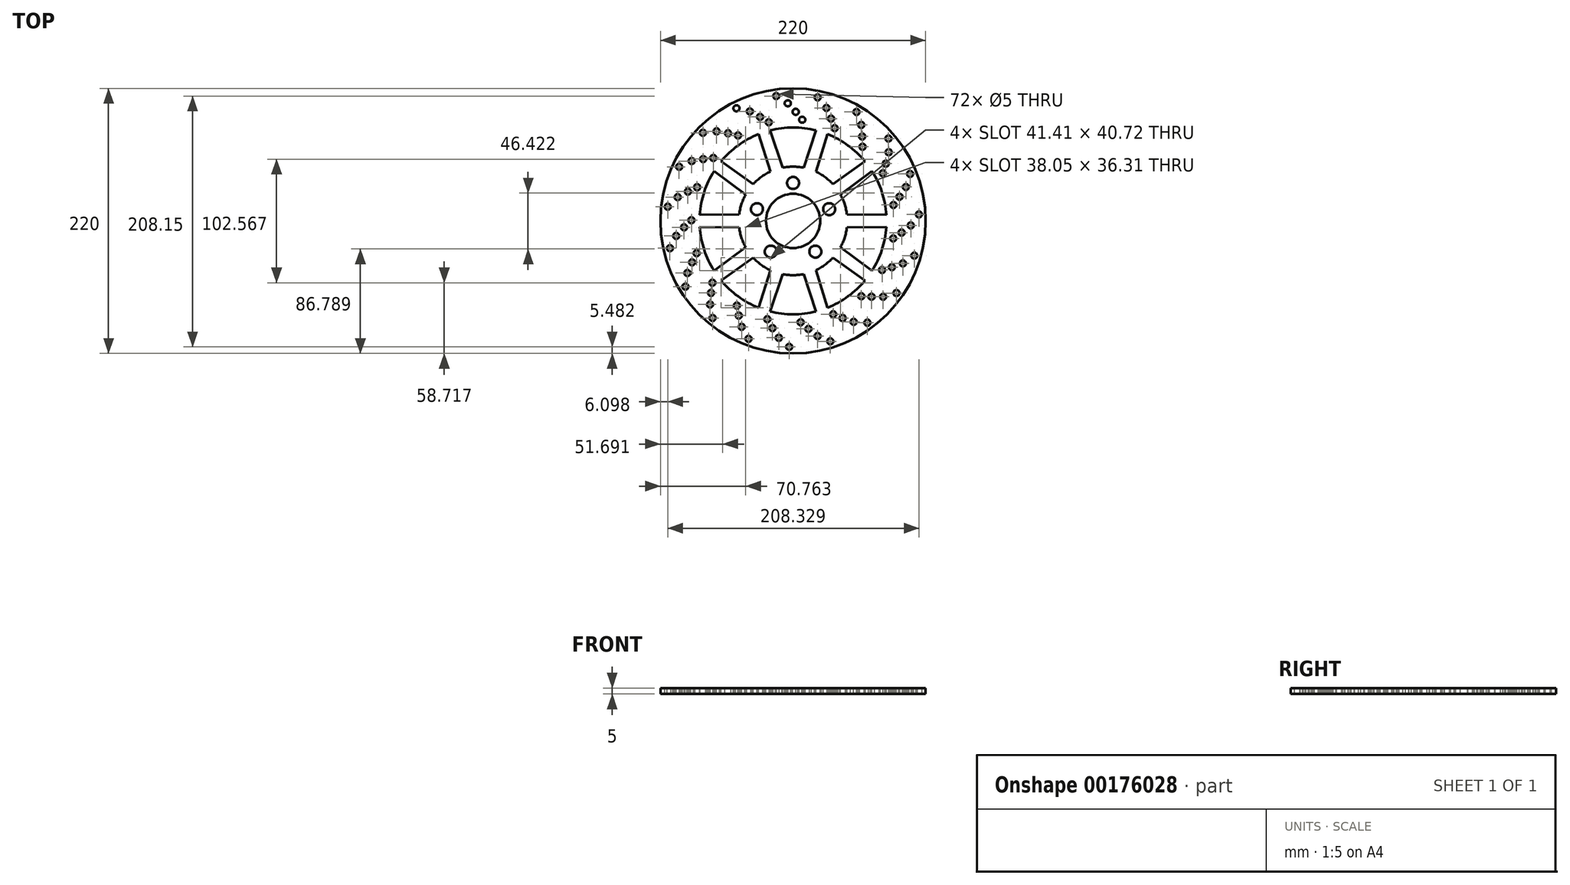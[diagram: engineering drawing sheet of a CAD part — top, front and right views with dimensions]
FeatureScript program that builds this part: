
annotation { "Feature Type Name" : "Feature", "Feature Type Description" : "" }
export const myFeature = defineFeature(function(context is Context, id is Id, definition is map)
    precondition{}
    {
        {
            var Q0;
            Q0=qCreatedBy(makeId("Top.planeOp"),FACE);
            var sketch = newSketch(context, id + "F0", { "sketchPlane" : qUnion([Q0])});
            skCircle(sketch, "E0", {"center": v(0, 0) * mm, "radius": 110 * mm});
            skSolve(sketch);
        }
        {
            var Q0;
            Q0 = qSketchRegion(id + "F0", true);
            extrude(context, id + "F1", {"entities" : qUnion([Q0]), "depth" : 5 * mm});
        }
        {
            var Q0;
            Q0=makeQuery(id+"F1.opExtrude","CAP_FACE",FACE,{"disambiguationData":[OSD([sQuery(id+"F0.wireOp",EDGE,"E0")])],"isStart":false});
            var sketch = newSketch(context, id + "F2", { "sketchPlane" : qUnion([Q0])});
            skArc(sketch, "E1", {"start": v(-28.04, 14.35) * mm, "mid": v(-29.96, 9.73) * mm, "end": v(-31.12, 4.87) * mm});
            skCircle(sketch, "E2", {"center": v(0, 31.5) * mm, "radius": 5 * mm});
            skCircle(sketch, "E3.1.0", {"center": v(-29.96, 9.73) * mm, "radius": 5 * mm});
            skCircle(sketch, "E3.2.0", {"center": v(-18.52, -25.48) * mm, "radius": 5 * mm});
            skCircle(sketch, "E3.3.0", {"center": v(18.52, -25.48) * mm, "radius": 5 * mm});
            skCircle(sketch, "E3.4.0", {"center": v(29.96, 9.73) * mm, "radius": 5 * mm});
            skArc(sketch, "E4.trimOffspring", {"start": v(-22.31, -22.23) * mm, "mid": v(-18.52, -25.48) * mm, "end": v(-14.25, -28.1) * mm});
            skArc(sketch, "E5.trimOffspring", {"start": v(14.25, -28.1) * mm, "mid": v(18.52, -25.48) * mm, "end": v(22.31, -22.23) * mm});
            skArc(sketch, "E6.trimOffspring", {"start": v(31.12, 4.87) * mm, "mid": v(29.96, 9.73) * mm, "end": v(28.04, 14.35) * mm});
            skArc(sketch, "E7.trimOffspring", {"start": v(4.98, 31.1) * mm, "mid": v(0, 31.5) * mm, "end": v(-4.98, 31.1) * mm});
            skCircle(sketch, "E8", {"center": v(0, 0) * mm, "radius": 22.5 * mm});
            skSolve(sketch);
        }
        {
            var Q0;
            Q0 = qSketchRegion(id + "F2", true);
            extrude(context, id + "F3", {"entities" : qUnion([Q0]), "operationType" : NewBodyOperationType.REMOVE, "endBound" : BoundingType.THROUGH_ALL, "oppositeDirection" : true, "depth" : 25 * mm});
        }
        {
            var Q0;
            Q0=makeQuery(id+"F1.opExtrude","CAP_FACE",FACE,{"disambiguationData":[OSD([sQuery(id+"F0.wireOp",EDGE,"E0")])],"isStart":false});
            var sketch = newSketch(context, id + "F4", { "sketchPlane" : qUnion([Q0])});
            skArc(sketch, "E9", {"start": v(8.74, 44.14) * mm, "mid": v(0, 45) * mm, "end": v(-8.74, 44.14) * mm});
            skArc(sketch, "E10", {"start": v(19.1, 75.11) * mm, "mid": v(0, 77.5) * mm, "end": v(-19.1, 75.11) * mm});
            skLineSegment(sketch, "E11", {"start": v(-8.74, 44.14) * mm, "end": v(-19.1, 75.11) * mm});
            skLineSegment(sketch, "E12", {"start": v(8.74, 44.14) * mm, "end": v(19.1, 75.11) * mm});
            skLineSegment(sketch, "E13.1.0", {"start": v(-33.01, 30.58) * mm, "end": v(-59.6, 49.54) * mm});
            skArc(sketch, "E13.1.1", {"start": v(-28.7, 71.99) * mm, "mid": v(-45.55, 62.7) * mm, "end": v(-59.6, 49.54) * mm});
            skLineSegment(sketch, "E13.1.2", {"start": v(-18.88, 40.85) * mm, "end": v(-28.7, 71.99) * mm});
            skArc(sketch, "E13.1.3", {"start": v(-18.88, 40.85) * mm, "mid": v(-26.45, 36.4) * mm, "end": v(-33.01, 30.58) * mm});
            skLineSegment(sketch, "E13.2.0", {"start": v(-44.68, 5.33) * mm, "end": v(-77.34, 5.05) * mm});
            skArc(sketch, "E13.2.1", {"start": v(-65.54, 41.37) * mm, "mid": v(-73.7, 23.95) * mm, "end": v(-77.34, 5.05) * mm});
            skLineSegment(sketch, "E13.2.2", {"start": v(-39.28, 21.95) * mm, "end": v(-65.54, 41.37) * mm});
            skArc(sketch, "E13.2.3", {"start": v(-39.28, 21.95) * mm, "mid": v(-42.8, 13.9) * mm, "end": v(-44.68, 5.33) * mm});
            skLineSegment(sketch, "E13.3.0", {"start": v(-39.28, -21.95) * mm, "end": v(-65.54, -41.37) * mm});
            skArc(sketch, "E13.3.1", {"start": v(-77.34, -5.05) * mm, "mid": v(-73.7, -23.95) * mm, "end": v(-65.54, -41.37) * mm});
            skLineSegment(sketch, "E13.3.2", {"start": v(-44.68, -5.33) * mm, "end": v(-77.34, -5.05) * mm});
            skArc(sketch, "E13.3.3", {"start": v(-44.68, -5.33) * mm, "mid": v(-42.8, -13.9) * mm, "end": v(-39.28, -21.95) * mm});
            skLineSegment(sketch, "E13.4.0", {"start": v(-18.88, -40.85) * mm, "end": v(-28.7, -71.99) * mm});
            skArc(sketch, "E13.4.1", {"start": v(-59.6, -49.54) * mm, "mid": v(-45.55, -62.7) * mm, "end": v(-28.7, -71.99) * mm});
            skLineSegment(sketch, "E13.4.2", {"start": v(-33.01, -30.58) * mm, "end": v(-59.6, -49.54) * mm});
            skArc(sketch, "E13.4.3", {"start": v(-33.01, -30.58) * mm, "mid": v(-26.45, -36.4) * mm, "end": v(-18.88, -40.85) * mm});
            skLineSegment(sketch, "E13.5.0", {"start": v(8.74, -44.14) * mm, "end": v(19.1, -75.11) * mm});
            skArc(sketch, "E13.5.1", {"start": v(-19.1, -75.11) * mm, "mid": v(0, -77.5) * mm, "end": v(19.1, -75.11) * mm});
            skLineSegment(sketch, "E13.5.2", {"start": v(-8.74, -44.14) * mm, "end": v(-19.1, -75.11) * mm});
            skArc(sketch, "E13.5.3", {"start": v(-8.74, -44.14) * mm, "mid": v(0, -45) * mm, "end": v(8.74, -44.14) * mm});
            skLineSegment(sketch, "E13.6.0", {"start": v(33.01, -30.58) * mm, "end": v(59.6, -49.54) * mm});
            skArc(sketch, "E13.6.1", {"start": v(28.7, -71.99) * mm, "mid": v(45.55, -62.7) * mm, "end": v(59.6, -49.54) * mm});
            skLineSegment(sketch, "E13.6.2", {"start": v(18.88, -40.85) * mm, "end": v(28.7, -71.99) * mm});
            skArc(sketch, "E13.6.3", {"start": v(18.88, -40.85) * mm, "mid": v(26.45, -36.4) * mm, "end": v(33.01, -30.58) * mm});
            skLineSegment(sketch, "E13.7.0", {"start": v(44.68, -5.33) * mm, "end": v(77.34, -5.05) * mm});
            skArc(sketch, "E13.7.1", {"start": v(65.54, -41.37) * mm, "mid": v(73.7, -23.95) * mm, "end": v(77.34, -5.05) * mm});
            skLineSegment(sketch, "E13.7.2", {"start": v(39.28, -21.95) * mm, "end": v(65.54, -41.37) * mm});
            skArc(sketch, "E13.7.3", {"start": v(39.28, -21.95) * mm, "mid": v(42.8, -13.9) * mm, "end": v(44.68, -5.33) * mm});
            skLineSegment(sketch, "E13.8.0", {"start": v(39.28, 21.95) * mm, "end": v(65.54, 41.37) * mm});
            skArc(sketch, "E13.8.1", {"start": v(77.34, 5.05) * mm, "mid": v(73.7, 23.95) * mm, "end": v(65.54, 41.37) * mm});
            skLineSegment(sketch, "E13.8.2", {"start": v(44.68, 5.33) * mm, "end": v(77.34, 5.05) * mm});
            skArc(sketch, "E13.8.3", {"start": v(44.68, 5.33) * mm, "mid": v(42.8, 13.9) * mm, "end": v(39.28, 21.95) * mm});
            skLineSegment(sketch, "E13.9.0", {"start": v(18.88, 40.85) * mm, "end": v(28.7, 71.99) * mm});
            skArc(sketch, "E13.9.1", {"start": v(59.6, 49.54) * mm, "mid": v(45.55, 62.7) * mm, "end": v(28.7, 71.99) * mm});
            skLineSegment(sketch, "E13.9.2", {"start": v(33.01, 30.58) * mm, "end": v(59.6, 49.54) * mm});
            skArc(sketch, "E13.9.3", {"start": v(33.01, 30.58) * mm, "mid": v(26.45, 36.4) * mm, "end": v(18.88, 40.85) * mm});
            skSolve(sketch);
        }
        {
            var Q0;
            Q0 = qSketchRegion(id + "F4", true);
            extrude(context, id + "F5", {"entities" : qUnion([Q0]), "operationType" : NewBodyOperationType.REMOVE, "endBound" : BoundingType.THROUGH_ALL, "oppositeDirection" : true, "depth" : 25 * mm});
        }
        {
            var Q0;
            Q0=makeQuery(id+"F1.opExtrude","CAP_FACE",FACE,{"disambiguationData":[OSD([sQuery(id+"F0.wireOp",EDGE,"E0")])],"isStart":false});
            var sketch = newSketch(context, id + "F6", { "sketchPlane" : qUnion([Q0])});
            skCircle(sketch, "E14", {"center": v(-46.84, 93.5) * mm, "radius": 2.5 * mm});
            skCircle(sketch, "E15", {"center": v(-4.26, 97.6) * mm, "radius": 2.5 * mm});
            skCircle(sketch, "E16", {"center": v(2.27, 90.5) * mm, "radius": 2.5 * mm});
            skCircle(sketch, "E17", {"center": v(7.67, 83.96) * mm, "radius": 2.5 * mm});
            skCircle(sketch, "E18.1.0", {"center": v(-13.95, 103.63) * mm, "radius": 2.5 * mm});
            skCircle(sketch, "E18.1.1", {"center": v(27.65, 93.7) * mm, "radius": 2.5 * mm});
            skCircle(sketch, "E18.1.2", {"center": v(31.53, 84.86) * mm, "radius": 2.5 * mm});
            skCircle(sketch, "E18.1.3", {"center": v(34.51, 76.92) * mm, "radius": 2.5 * mm});
            skCircle(sketch, "E18.2.0", {"center": v(20.44, 102.55) * mm, "radius": 2.5 * mm});
            skCircle(sketch, "E18.2.1", {"center": v(56.57, 79.65) * mm, "radius": 2.5 * mm});
            skCircle(sketch, "E18.2.2", {"center": v(57.36, 70.03) * mm, "radius": 2.5 * mm});
            skCircle(sketch, "E18.2.3", {"center": v(57.61, 61.56) * mm, "radius": 2.5 * mm});
            skCircle(sketch, "E18.3.0", {"center": v(52.63, 90.36) * mm, "radius": 2.5 * mm});
            skCircle(sketch, "E18.3.1", {"center": v(79.36, 56.97) * mm, "radius": 2.5 * mm});
            skCircle(sketch, "E18.3.2", {"center": v(77, 47.62) * mm, "radius": 2.5 * mm});
            skCircle(sketch, "E18.3.3", {"center": v(74.47, 39.52) * mm, "radius": 2.5 * mm});
            skCircle(sketch, "E18.4.0", {"center": v(79.1, 68.38) * mm, "radius": 2.5 * mm});
            skCircle(sketch, "E18.4.1", {"center": v(93.56, 28.13) * mm, "radius": 2.5 * mm});
            skCircle(sketch, "E18.4.2", {"center": v(88.28, 20.04) * mm, "radius": 2.5 * mm});
            skCircle(sketch, "E18.4.3", {"center": v(83.27, 13.2) * mm, "radius": 2.5 * mm});
            skPoint(sketch, "E18.center", {"position": v(0, 0) * mm});
            skLineSegment(sketch, "E18.anchor1", {"start": v(0, 0) * mm, "end": v(-46.84, 93.5) * mm, "construction": true});
            skLineSegment(sketch, "E18.anchor2", {"start": v(0, 0) * mm, "end": v(-47, 93.4) * mm, "construction": true});
            skCircle(sketch, "E19.1.5.0", {"center": v(97.02, 39) * mm, "radius": 2.5 * mm});
            skCircle(sketch, "E19.2.5.0", {"center": v(97.62, -3.77) * mm, "radius": 2.5 * mm});
            skCircle(sketch, "E19.4.5.0", {"center": v(90, -9.7) * mm, "radius": 2.5 * mm});
            skCircle(sketch, "E19.6.5.0", {"center": v(83.05, -14.54) * mm, "radius": 2.5 * mm});
            skCircle(sketch, "E19.1.6.0", {"center": v(104.43, 5.4) * mm, "radius": 2.5 * mm});
            skCircle(sketch, "E19.2.6.0", {"center": v(91.11, -35.25) * mm, "radius": 2.5 * mm});
            skCircle(sketch, "E19.4.6.0", {"center": v(81.98, -38.39) * mm, "radius": 2.5 * mm});
            skCircle(sketch, "E19.6.6.0", {"center": v(73.83, -40.71) * mm, "radius": 2.5 * mm});
            skCircle(sketch, "E19.1.7.0", {"center": v(100.52, -28.8) * mm, "radius": 2.5 * mm});
            skCircle(sketch, "E19.2.7.0", {"center": v(74.73, -62.92) * mm, "radius": 2.5 * mm});
            skCircle(sketch, "E19.4.7.0", {"center": v(65.08, -62.92) * mm, "radius": 2.5 * mm});
            skCircle(sketch, "E19.6.7.0", {"center": v(56.62, -62.47) * mm, "radius": 2.5 * mm});
            skCircle(sketch, "E19.1.8.0", {"center": v(85.73, -59.87) * mm, "radius": 2.5 * mm});
            skCircle(sketch, "E19.2.8.0", {"center": v(50.26, -83.77) * mm, "radius": 2.5 * mm});
            skCircle(sketch, "E19.4.8.0", {"center": v(41.13, -80.64) * mm, "radius": 2.5 * mm});
            skCircle(sketch, "E19.6.8.0", {"center": v(33.27, -77.47) * mm, "radius": 2.5 * mm});
            skCircle(sketch, "E19.1.9.0", {"center": v(61.66, -84.46) * mm, "radius": 2.5 * mm});
            skCircle(sketch, "E19.2.9.0", {"center": v(20.35, -95.55) * mm, "radius": 2.5 * mm});
            skCircle(sketch, "E19.4.9.0", {"center": v(12.73, -89.63) * mm, "radius": 2.5 * mm});
            skCircle(sketch, "E19.6.9.0", {"center": v(6.32, -84.07) * mm, "radius": 2.5 * mm});
            skCircle(sketch, "E19.1.10.0", {"center": v(30.9, -99.9) * mm, "radius": 2.5 * mm});
            skCircle(sketch, "E19.2.10.0", {"center": v(-11.77, -96.98) * mm, "radius": 2.5 * mm});
            skCircle(sketch, "E19.4.10.0", {"center": v(-17.06, -88.9) * mm, "radius": 2.5 * mm});
            skCircle(sketch, "E19.6.10.0", {"center": v(-21.31, -81.57) * mm, "radius": 2.5 * mm});
            skCircle(sketch, "E19.1.11.0", {"center": v(-3.2, -104.52) * mm, "radius": 2.5 * mm});
            skCircle(sketch, "E19.2.11.0", {"center": v(-42.62, -87.9) * mm, "radius": 2.5 * mm});
            skCircle(sketch, "E19.4.11.0", {"center": v(-45, -78.55) * mm, "radius": 2.5 * mm});
            skCircle(sketch, "E19.6.11.0", {"center": v(-46.64, -70.24) * mm, "radius": 2.5 * mm});
            skCircle(sketch, "E19.1.12.0", {"center": v(-36.95, -97.82) * mm, "radius": 2.5 * mm});
            skCircle(sketch, "E19.2.12.0", {"center": v(-68.84, -69.31) * mm, "radius": 2.5 * mm});
            skCircle(sketch, "E19.4.12.0", {"center": v(-68.05, -59.7) * mm, "radius": 2.5 * mm});
            skCircle(sketch, "E19.6.12.0", {"center": v(-66.91, -51.3) * mm, "radius": 2.5 * mm});
            skCircle(sketch, "E19.1.13.0", {"center": v(-66.7, -80.53) * mm, "radius": 2.5 * mm});
            skCircle(sketch, "E19.2.13.0", {"center": v(-87.62, -43.21) * mm, "radius": 2.5 * mm});
            skCircle(sketch, "E19.4.13.0", {"center": v(-83.75, -34.37) * mm, "radius": 2.5 * mm});
            skCircle(sketch, "E19.6.13.0", {"center": v(-79.94, -26.8) * mm, "radius": 2.5 * mm});
            skCircle(sketch, "E19.1.14.0", {"center": v(-89.23, -54.51) * mm, "radius": 2.5 * mm});
            skCircle(sketch, "E19.2.14.0", {"center": v(-96.9, -12.43) * mm, "radius": 2.5 * mm});
            skCircle(sketch, "E19.4.14.0", {"center": v(-90.37, -5.32) * mm, "radius": 2.5 * mm});
            skCircle(sketch, "E19.6.14.0", {"center": v(-84.3, 0.6) * mm, "radius": 2.5 * mm});
            skCircle(sketch, "E19.1.15.0", {"center": v(-102.1, -22.6) * mm, "radius": 2.5 * mm});
            skCircle(sketch, "E19.2.15.0", {"center": v(-95.69, 19.7) * mm, "radius": 2.5 * mm});
            skCircle(sketch, "E19.4.15.0", {"center": v(-87.2, 24.3) * mm, "radius": 2.5 * mm});
            skCircle(sketch, "E19.6.15.0", {"center": v(-79.55, 27.94) * mm, "radius": 2.5 * mm});
            skCircle(sketch, "E19.1.16.0", {"center": v(-103.9, 11.77) * mm, "radius": 2.5 * mm});
            skCircle(sketch, "E19.2.16.0", {"center": v(-84.11, 49.7) * mm, "radius": 2.5 * mm});
            skCircle(sketch, "E19.4.16.0", {"center": v(-74.6, 51.3) * mm, "radius": 2.5 * mm});
            skCircle(sketch, "E19.6.16.0", {"center": v(-66.17, 52.25) * mm, "radius": 2.5 * mm});
            skCircle(sketch, "E19.1.17.0", {"center": v(-94.45, 44.86) * mm, "radius": 2.5 * mm});
            skCircle(sketch, "E19.2.17.0", {"center": v(-63.43, 74.3) * mm, "radius": 2.5 * mm});
            skCircle(sketch, "E19.4.17.0", {"center": v(-53.9, 72.73) * mm, "radius": 2.5 * mm});
            skCircle(sketch, "E19.6.17.0", {"center": v(-45.63, 70.9) * mm, "radius": 2.5 * mm});
            skCircle(sketch, "E19.1.18.0", {"center": v(-74.78, 73.1) * mm, "radius": 2.5 * mm});
            skCircle(sketch, "E19.2.18.0", {"center": v(-35.87, 90.87) * mm, "radius": 2.5 * mm});
            skCircle(sketch, "E19.4.18.0", {"center": v(-27.38, 86.29) * mm, "radius": 2.5 * mm});
            skCircle(sketch, "E19.6.18.0", {"center": v(-20.14, 81.87) * mm, "radius": 2.5 * mm});
            skCircle(sketch, "E19.1.19.0", {"center": v(-47, 93.4) * mm, "radius": 2.5 * mm});
            skCircle(sketch, "E19.2.19.0", {"center": v(-4.43, 97.6) * mm, "radius": 2.5 * mm});
            skCircle(sketch, "E19.4.19.0", {"center": v(2.12, 90.5) * mm, "radius": 2.5 * mm});
            skCircle(sketch, "E19.6.19.0", {"center": v(7.53, 83.97) * mm, "radius": 2.5 * mm});
            skSolve(sketch);
        }
        {
            var Q0;
            Q0 = qSketchRegion(id + "F6", true);
            extrude(context, id + "F7", {"entities" : qUnion([Q0]), "operationType" : NewBodyOperationType.REMOVE, "endBound" : BoundingType.THROUGH_ALL, "oppositeDirection" : true, "depth" : 25 * mm});
        }
    });
